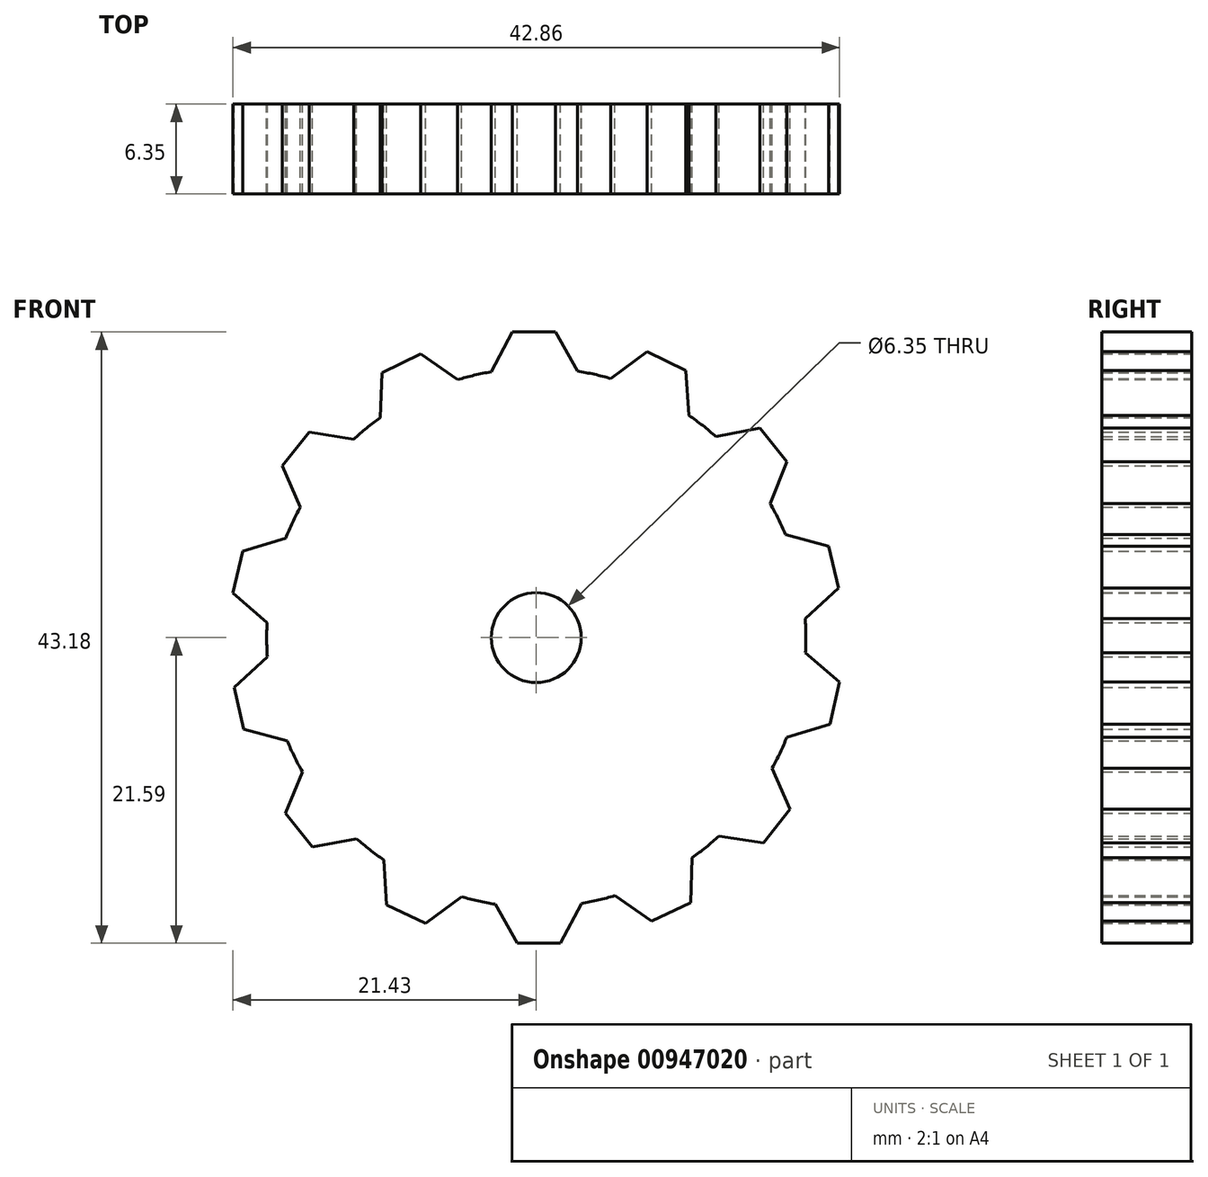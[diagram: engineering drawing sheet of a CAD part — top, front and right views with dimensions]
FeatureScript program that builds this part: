
annotation { "Feature Type Name" : "Feature", "Feature Type Description" : "" }
export const myFeature = defineFeature(function(context is Context, id is Id, definition is map)
    precondition{}
    {
        {
            var Q0;
            Q0=qCreatedBy(makeId("Front.planeOp"),FACE);
            var sketch = newSketch(context, id + "F0", { "sketchPlane" : qUnion([Q0])});
            skCircle(sketch, "E0", {"center": v(0, 0) * mm, "radius": 19.05 * mm});
            skLineSegment(sketch, "E1", {"start": v(2.9, 18.83) * mm, "end": v(1.34, 21.59) * mm});
            skLineSegment(sketch, "E2", {"start": v(-1.7, 21.59) * mm, "end": v(-3.19, 18.78) * mm});
            skPoint(sketch, "E3", {"position": v(0, 19.05) * mm});
            skPoint(sketch, "E4.center", {"position": v(-0.4, 2.05) * mm});
            skLineSegment(sketch, "E5", {"start": v(-1.7, 21.59) * mm, "end": v(1.34, 21.59) * mm});
            skLineSegment(sketch, "E6.1.0", {"start": v(-10.9, 18.71) * mm, "end": v(-8.16, 20.03) * mm});
            skLineSegment(sketch, "E6.1.1", {"start": v(-10.9, 18.71) * mm, "end": v(-11.02, 15.54) * mm});
            skLineSegment(sketch, "E6.1.2", {"start": v(-5.55, 18.22) * mm, "end": v(-8.16, 20.03) * mm});
            skLineSegment(sketch, "E6.2.0", {"start": v(-17.94, 12.13) * mm, "end": v(-16.04, 14.5) * mm});
            skLineSegment(sketch, "E6.2.1", {"start": v(-17.94, 12.13) * mm, "end": v(-16.67, 9.22) * mm});
            skLineSegment(sketch, "E6.2.2", {"start": v(-12.9, 14) * mm, "end": v(-16.04, 14.5) * mm});
            skLineSegment(sketch, "E6.3.0", {"start": v(-21.43, 3.14) * mm, "end": v(-20.75, 6.11) * mm});
            skLineSegment(sketch, "E6.3.1", {"start": v(-21.43, 3.14) * mm, "end": v(-19.02, 1.07) * mm});
            skLineSegment(sketch, "E6.3.2", {"start": v(-17.7, 7.02) * mm, "end": v(-20.75, 6.11) * mm});
            skLineSegment(sketch, "E6.4.0", {"start": v(-20.67, -6.47) * mm, "end": v(-21.35, -3.5) * mm});
            skLineSegment(sketch, "E6.4.1", {"start": v(-20.67, -6.47) * mm, "end": v(-17.6, -7.29) * mm});
            skLineSegment(sketch, "E6.4.2", {"start": v(-19, -1.36) * mm, "end": v(-21.35, -3.5) * mm});
            skLineSegment(sketch, "E6.5.0", {"start": v(-15.82, -14.8) * mm, "end": v(-17.72, -12.41) * mm});
            skLineSegment(sketch, "E6.5.1", {"start": v(-15.82, -14.8) * mm, "end": v(-12.7, -14.2) * mm});
            skLineSegment(sketch, "E6.5.2", {"start": v(-16.53, -9.47) * mm, "end": v(-17.72, -12.41) * mm});
            skLineSegment(sketch, "E6.6.0", {"start": v(-7.83, -20.2) * mm, "end": v(-10.58, -18.87) * mm});
            skLineSegment(sketch, "E6.6.1", {"start": v(-7.83, -20.2) * mm, "end": v(-5.28, -18.3) * mm});
            skLineSegment(sketch, "E6.6.2", {"start": v(-10.79, -15.7) * mm, "end": v(-10.58, -18.87) * mm});
            skLineSegment(sketch, "E6.7.0", {"start": v(1.7, -21.59) * mm, "end": v(-1.34, -21.59) * mm});
            skLineSegment(sketch, "E6.7.1", {"start": v(1.7, -21.59) * mm, "end": v(3.19, -18.78) * mm});
            skLineSegment(sketch, "E6.7.2", {"start": v(-2.9, -18.83) * mm, "end": v(-1.34, -21.59) * mm});
            skLineSegment(sketch, "E6.8.0", {"start": v(10.9, -18.71) * mm, "end": v(8.16, -20.03) * mm});
            skLineSegment(sketch, "E6.8.1", {"start": v(10.9, -18.71) * mm, "end": v(11.02, -15.54) * mm});
            skLineSegment(sketch, "E6.8.2", {"start": v(5.55, -18.22) * mm, "end": v(8.16, -20.03) * mm});
            skLineSegment(sketch, "E6.9.0", {"start": v(17.94, -12.13) * mm, "end": v(16.04, -14.5) * mm});
            skLineSegment(sketch, "E6.9.1", {"start": v(17.94, -12.13) * mm, "end": v(16.67, -9.22) * mm});
            skLineSegment(sketch, "E6.9.2", {"start": v(12.9, -14) * mm, "end": v(16.04, -14.5) * mm});
            skLineSegment(sketch, "E6.10.0", {"start": v(21.43, -3.14) * mm, "end": v(20.75, -6.11) * mm});
            skLineSegment(sketch, "E6.10.1", {"start": v(21.43, -3.14) * mm, "end": v(19.02, -1.07) * mm});
            skLineSegment(sketch, "E6.10.2", {"start": v(17.7, -7.02) * mm, "end": v(20.75, -6.11) * mm});
            skLineSegment(sketch, "E6.11.0", {"start": v(20.67, 6.47) * mm, "end": v(21.35, 3.5) * mm});
            skLineSegment(sketch, "E6.11.1", {"start": v(20.67, 6.47) * mm, "end": v(17.6, 7.29) * mm});
            skLineSegment(sketch, "E6.11.2", {"start": v(19, 1.36) * mm, "end": v(21.35, 3.5) * mm});
            skLineSegment(sketch, "E6.12.0", {"start": v(15.82, 14.8) * mm, "end": v(17.72, 12.41) * mm});
            skLineSegment(sketch, "E6.12.1", {"start": v(15.82, 14.8) * mm, "end": v(12.7, 14.2) * mm});
            skLineSegment(sketch, "E6.12.2", {"start": v(16.53, 9.47) * mm, "end": v(17.72, 12.41) * mm});
            skLineSegment(sketch, "E6.13.0", {"start": v(7.83, 20.2) * mm, "end": v(10.58, 18.87) * mm});
            skLineSegment(sketch, "E6.13.1", {"start": v(7.83, 20.2) * mm, "end": v(5.28, 18.3) * mm});
            skLineSegment(sketch, "E6.13.2", {"start": v(10.79, 15.7) * mm, "end": v(10.58, 18.87) * mm});
            skCircle(sketch, "E7", {"center": v(0, 0) * mm, "radius": 3.18 * mm});
            skSolve(sketch);
        }
        {
            var Q0;
            Q0 = qSketchRegion(id + "F0", true);
            extrude(context, id + "F1", {"entities" : qUnion([Q0]), "depth" : 6.35 * mm, "offsetDistance" : 25.4 * mm});
        }
    });
